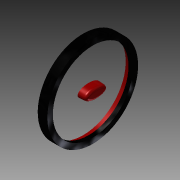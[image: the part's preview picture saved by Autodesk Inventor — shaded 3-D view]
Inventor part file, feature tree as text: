
AUTODESK INVENTOR PART (.ipt)
format: ipt  version: 2014 (Build 180170000, 170)  size: 658,432 bytes
history: native  units: in
note: dims shown in document units (in); Inventor stores cm internally (conversion verified against a paired STEP export)
features: sketch x23, extrude x17, plane x9, projected_geometry x5, loft x4, other x3, mirror x1, emboss x1, fillet x1
ambient origin geometry x8: Origin, YZ Plane, XZ Plane, XY Plane, X Axis, Y Axis, Z Axis, Center Point
bodies: Solid1 (feature_tree)
feature tree (64):
  sketch  "Sketch1"  dims[d0=0.7559in d1=0.7559in]
  plane  "Work Plane1"
  loft  "Loft1"
  extrude  "Extrusion1"  Depth=0.2in
  plane  "Work Plane4"
  loft  "Loft2"
  plane  "Work Plane5"
  loft  "Loft3"
  loft  "Loft4"
  extrude  "Extrusion2"  TaperAngle=0.0deg  [1 undecoded]
  plane  "Work Plane6"
  extrude  "Extrusion3"  Depth=1.0in
  extrude  "Extrusion4"  Depth=1.0651in
  extrude  "Extrusion5"  Depth=0.962in
  plane  "Work Plane7"
  extrude  "Extrusion6"  Depth=0.075in
  plane  "Work Plane8"
  other  "Work Axis1"
  plane  "Work Plane9"
  extrude  "Extrusion7"  Depth=0.06in
  mirror  "Mirror3"
  extrude  "Extrusion8"  Depth=0.05in
  plane  "Work Plane10"
  extrude  "Extrusion9"  Depth=0.0625in
  plane  "Work Plane11"
  extrude  "Extrusion10"  Depth=0.075in
  extrude  "Extrusion11"  TaperAngle=0.0deg  [1 undecoded]
  extrude  "Extrusion12"  Depth=0.2in
  extrude  "Extrusion13"  TaperAngle=0.0deg  [1 undecoded]
  emboss  "Emboss1"
  extrude  "Extrusion16"  Depth=0.01in
  extrude  "Extrusion17"  Depth=0.0344in
  extrude  "Extrusion18"  TaperAngle=60.0deg  [1 undecoded]
  fillet  "Fillet1"  [1 undecoded]
  extrude  "Extrusion20"  Depth=0.05in
  sketch  "Sketch2"  dims[d2=0.9963in d3=0.2in]
  sketch  "Sketch3"  dims[d4=0.5in d6=0.08in]
  sketch  "Sketch4"  dims[d7=0.55in d8=150.0deg]
  other  "Edges1"
  sketch  "Sketch5"  dims[d9=150.0deg d14=0.33in]
  projected_geometry  "Projected Loop1"
  other  "Edges2"
  sketch  "Sketch6"  dims[d15=0.66in d18=0.0in d19=90.0deg]
  sketch  "Sketch7"  dims[d20=0.0in d21=90.0deg d22=1.0in]
  sketch  "Sketch8"  dims[d26=1.0651in d28=1.0651in]
  sketch  "Sketch9"  dims[d29=0.0in d30=0.962in]
  sketch  "Sketch10"  dims[d31=0.962in d32=0.075in]
  sketch  "Sketch11"  dims[d33=0.15in d34=0.06in]
  sketch  "Sketch12"  dims[d35=0.1in d36=0.05in]
  sketch  "Sketch13"  dims[d37=0.45in d38=0.0in d39=0.0625in]
  projected_geometry  "Projected Loop2"
  projected_geometry  "Projected Loop3"
  sketch  "Sketch14"  dims[d40=0.01in d41=0.075in]
  projected_geometry  "Projected Loop4"
  sketch  "Sketch15"  dims[d42=0.01in d43=0.0in d44=90.0deg]
  sketch  "Sketch16"  dims[d45=0.0in d46=90.0deg d47=0.2in]
  sketch  "Sketch17"  dims[d48=0.07in d49=0.0in d50=90.0deg]
  sketch  "Sketch18"  dims[d51=0.0in d52=90.0deg d53=0.01in]
  sketch  "Sketch19"  dims[d54=0.01in d55=0.0344in]
  sketch  "Sketch23"  dims[d56=150.0deg d57=60.0deg d58=150.0deg]
  projected_geometry  "Projected Loop6"
  sketch  "Sketch24"  dims[d59=0.7in d60=0.05in]
  sketch  "Sketch25"  dims[d61=0.05in d62=0.05in]
  sketch  "Sketch27"  dims[d63=0.05in d64=0.05in d65=0.01in d66=0.0in d67=90.0deg d68=0.0in d69=90.0deg d70=0.1in d71=0.4in d72=0.15in d73=0.05in d74=0.0in d75=0.02in d77=0.15in d78=0.02in d79=0.1in d80=0.1in d81=0.1in d82=0.02in d83=0.15in d84=0.05in d85=0.0in d86=0.045in d87=0.0in d88=0.025in d89=0.0in d90=0.02in d91=0.02in d92=0.005in d93=0.0in d94=90.0deg d95=0.4466in d96=1.0in d97=0.0in d98=1.0in d99=0.0in d100=0.6528in d101=0.0in d102=0.0in d103=1.0in d104=0.0in d106=90.0deg d107=1.0in d108=0.0in d109=1.65in d110=0.1in d111=0.1in d112=0.0in d113=0.1in d114=0.075in d115=0.0in d116=0.05in d117=0.0in d123=0.84in d124=0.8in d125=0.0in d126=0.0in d127=1.0in d128=0.0in d130=0.15in d131=-0.0206in d135=0.2in d136=0.05in d137=0.1in d140=0.05in d141=0.1in d142=0.0in]
note: 5 required parameter values undecoded (feature->parameter linkage not recoverable at this tier; creation-order binding heuristic only, values carry confidence <= 0.55)
